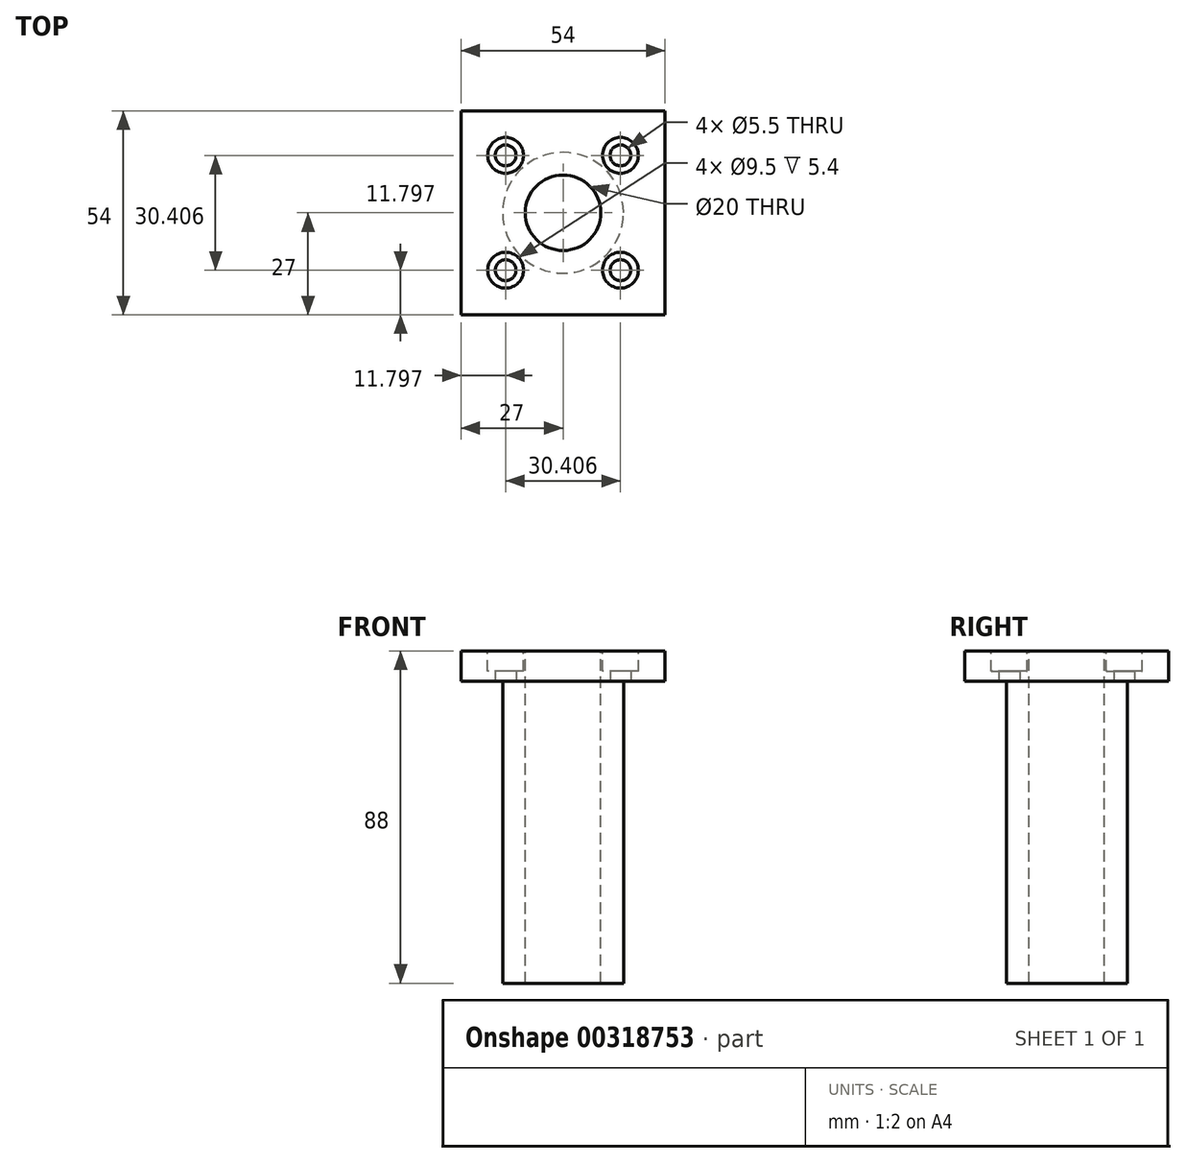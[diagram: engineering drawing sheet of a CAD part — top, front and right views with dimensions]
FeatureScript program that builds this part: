
annotation { "Feature Type Name" : "Feature", "Feature Type Description" : "" }
export const myFeature = defineFeature(function(context is Context, id is Id, definition is map)
    precondition{}
    {
        {
            var Q0;
            Q0=qCreatedBy(makeId("Top.planeOp"),FACE);
            var sketch = newSketch(context, id + "F0", { "sketchPlane" : qUnion([Q0])});
            skLineSegment(sketch, "E0.bottom", {"start": v(27, 27) * mm, "end": v(-27, 27) * mm});
            skLineSegment(sketch, "E0.top", {"start": v(27, -27) * mm, "end": v(-27, -27) * mm});
            skLineSegment(sketch, "E0.left", {"start": v(27, 27) * mm, "end": v(27, -27) * mm});
            skLineSegment(sketch, "E0.right", {"start": v(-27, 27) * mm, "end": v(-27, -27) * mm});
            skPoint(sketch, "E0.middle", {"position": v(0, 0) * mm});
            skCircle(sketch, "E1", {"center": v(0, 0) * mm, "radius": 21.5 * mm, "construction": true});
            skLineSegment(sketch, "E2.bottom", {"start": v(15.2, 15.2) * mm, "end": v(-15.2, 15.2) * mm, "construction": true});
            skLineSegment(sketch, "E2.top", {"start": v(15.2, -15.2) * mm, "end": v(-15.2, -15.2) * mm, "construction": true});
            skLineSegment(sketch, "E2.left", {"start": v(15.2, 15.2) * mm, "end": v(15.2, -15.2) * mm, "construction": true});
            skLineSegment(sketch, "E2.right", {"start": v(-15.2, 15.2) * mm, "end": v(-15.2, -15.2) * mm, "construction": true});
            skCircle(sketch, "E3", {"center": v(-15.2, 15.2) * mm, "radius": 2.75 * mm});
            skCircle(sketch, "E4", {"center": v(15.2, 15.2) * mm, "radius": 2.75 * mm});
            skCircle(sketch, "E5", {"center": v(15.2, -15.2) * mm, "radius": 2.75 * mm});
            skCircle(sketch, "E6", {"center": v(-15.2, -15.2) * mm, "radius": 2.75 * mm});
            skSolve(sketch);
        }
        {
            var Q0;
            Q0=makeQuery(id+"F0.imprint","IMPRINT",FACE,{"disambiguationData":[TD([[makeQuery(id+"F0.imprint","IMPRINT",EDGE,{"derivedFrom":sQuery(id+"F0.wireOp",EDGE,"E0.bottom")}),1.0]])]});
            extrude(context, id + "F1", {"entities" : qUnion([Q0]), "depth" : 8 * mm, "offsetDistance" : 25 * mm});
        }
        {
            var Q0;
            Q0=makeQuery(id+"F1.opExtrude","CAP_FACE",FACE,{"disambiguationData":[OSD([sQuery(id+"F0.wireOp",EDGE,"E0.bottom"),sQuery(id+"F0.wireOp",EDGE,"E0.top"),sQuery(id+"F0.wireOp",EDGE,"E0.left"),sQuery(id+"F0.wireOp",EDGE,"E0.right"),sQuery(id+"F0.wireOp",EDGE,"E3"),sQuery(id+"F0.wireOp",EDGE,"E4"),sQuery(id+"F0.wireOp",EDGE,"E5"),sQuery(id+"F0.wireOp",EDGE,"E6")])],"isStart":true});
            var sketch = newSketch(context, id + "F2", { "sketchPlane" : qUnion([Q0])});
            skCircle(sketch, "E7", {"center": v(0, 0) * mm, "radius": 16 * mm});
            skCircle(sketch, "E8", {"center": v(0, 0) * mm, "radius": 10 * mm});
            skSolve(sketch);
        }
        {
            var Q0;
            Q0=makeQuery(id+"F2.imprint","IMPRINT",FACE,{"disambiguationData":[TD([[makeQuery(id+"F2.imprint","IMPRINT",EDGE,{"derivedFrom":sQuery(id+"F2.wireOp",EDGE,"E7")}),1.0]])]});
            extrude(context, id + "F3", {"entities" : qUnion([Q0]), "operationType" : NewBodyOperationType.ADD, "depth" : 80 * mm, "offsetDistance" : 25 * mm});
        }
        {
            var Q0;
            Q0=makeQuery(id+"F1.opExtrude","CAP_FACE",FACE,{"disambiguationData":[OSD([sQuery(id+"F0.wireOp",EDGE,"E0.bottom"),sQuery(id+"F0.wireOp",EDGE,"E0.top"),sQuery(id+"F0.wireOp",EDGE,"E0.left"),sQuery(id+"F0.wireOp",EDGE,"E0.right"),sQuery(id+"F0.wireOp",EDGE,"E3"),sQuery(id+"F0.wireOp",EDGE,"E4"),sQuery(id+"F0.wireOp",EDGE,"E5"),sQuery(id+"F0.wireOp",EDGE,"E6")])],"isStart":false});
            var sketch = newSketch(context, id + "F4", { "sketchPlane" : qUnion([Q0])});
            skCircle(sketch, "E9", {"center": v(-15.2, 15.2) * mm, "radius": 4.75 * mm});
            skCircle(sketch, "E10", {"center": v(15.2, 15.2) * mm, "radius": 4.75 * mm});
            skCircle(sketch, "E11", {"center": v(15.2, -15.2) * mm, "radius": 4.75 * mm});
            skCircle(sketch, "E12", {"center": v(-15.2, -15.2) * mm, "radius": 4.75 * mm});
            skSolve(sketch);
        }
        {
            var Q0;
            Q0 = qSketchRegion(id + "F4", true);
            extrude(context, id + "F5", {"entities" : qUnion([Q0]), "operationType" : NewBodyOperationType.REMOVE, "oppositeDirection" : true, "depth" : 5.4 * mm, "offsetDistance" : 25 * mm});
        }
        {
            var Q0;
            Q0=makeQuery(id+"F1.opExtrude","CAP_FACE",FACE,{"disambiguationData":[OSD([sQuery(id+"F0.wireOp",EDGE,"E0.bottom"),sQuery(id+"F0.wireOp",EDGE,"E0.top"),sQuery(id+"F0.wireOp",EDGE,"E0.left"),sQuery(id+"F0.wireOp",EDGE,"E0.right"),sQuery(id+"F0.wireOp",EDGE,"E3"),sQuery(id+"F0.wireOp",EDGE,"E4"),sQuery(id+"F0.wireOp",EDGE,"E5"),sQuery(id+"F0.wireOp",EDGE,"E6")])],"isStart":false});
            var sketch = newSketch(context, id + "F6", { "sketchPlane" : qUnion([Q0])});
            skCircle(sketch, "E13", {"center": v(0, 0) * mm, "radius": 10 * mm});
            skSolve(sketch);
        }
        {
            var Q0;
            Q0=makeQuery(id+"F6.imprint","IMPRINT",FACE,{"disambiguationData":[TD([[makeQuery(id+"F6.imprint","IMPRINT",EDGE,{"derivedFrom":sQuery(id+"F6.wireOp",EDGE,"E13")}),1.0]])]});
            extrude(context, id + "F7", {"entities" : qUnion([Q0]), "operationType" : NewBodyOperationType.REMOVE, "oppositeDirection" : true, "depth" : 25 * mm, "offsetDistance" : 25 * mm});
        }
    });
